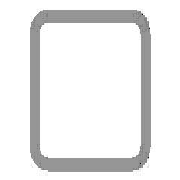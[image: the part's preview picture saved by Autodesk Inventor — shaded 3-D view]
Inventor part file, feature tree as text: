
AUTODESK INVENTOR PART (.ipt)
format: ipt  version: 2022 (Build 260153000, 153)  size: 154,112 bytes
history: native  units: mm (DEFAULTED — no unit token found)
features: other x4, plane x3, sketch x3, split x2, extrude x1
ambient origin geometry x8: Origin, YZ Plane, XZ Plane, XY Plane, X Axis, Y Axis, Z Axis, Center Point
bodies: Solid1 (feature_tree)
feature tree (13):
  parser-record x1  (decoder bookkeeping rows leaked as tree rows — omitted from the tree; the rows remain in map.json)
  other  "Driven Length"
  other  "Plano inicial"
  other  "Plano final"
  extrude  "Cuerpo"  TaperAngle=0.0deg  [1 undecoded]
  plane  "Plano de trabajo4"
  split  "Dividir1"
  plane  "Plano de trabajo5"
  split  "Dividir2"
  sketch  "Boceto"  dims[d10=40.0mm d11=40.0mm d12=5.0mm d13=-20.0mm d14=305.182521mm d15=20.0mm d16=20.0mm d17=90.0deg d18=325.182521mm]
  sketch  "Sketch3"  dims[d3=325.182521mm d4=0.0mm]
  plane  "Work Plane3"
  sketch  "Sketch4"  dims[d7=7.5mm]
note: 1 required parameter value undecoded (feature->parameter linkage not recoverable at this tier; creation-order binding heuristic only, values carry confidence <= 0.55)
